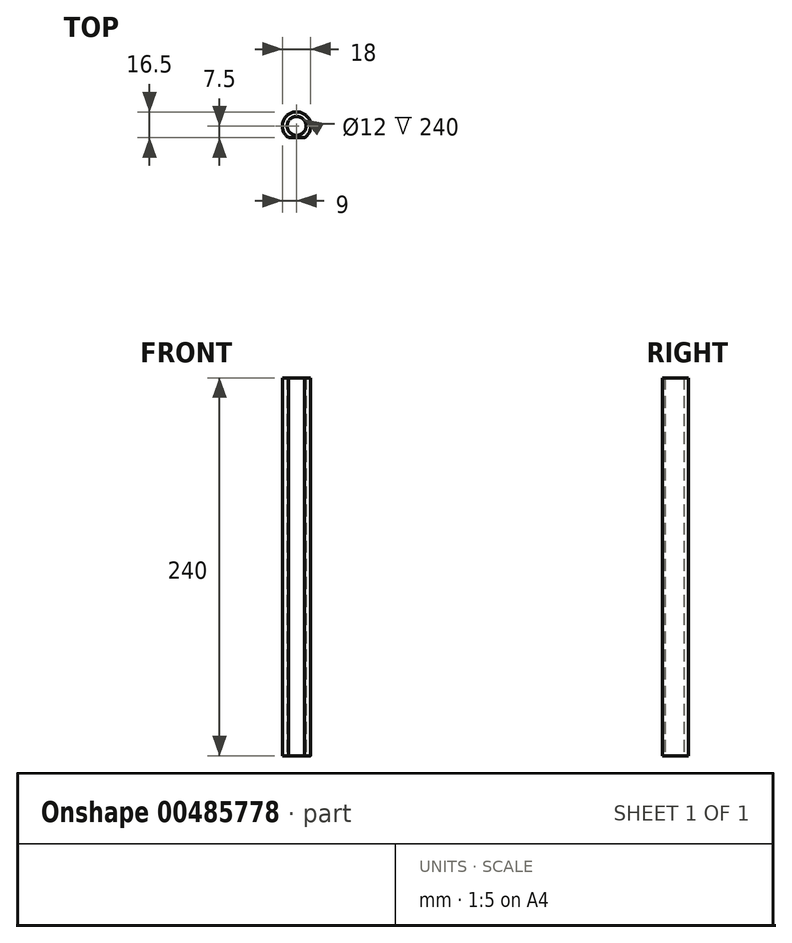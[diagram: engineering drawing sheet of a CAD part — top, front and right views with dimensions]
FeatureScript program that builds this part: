
annotation { "Feature Type Name" : "Feature", "Feature Type Description" : "" }
export const myFeature = defineFeature(function(context is Context, id is Id, definition is map)
    precondition{}
    {
        {
            var Q0;
            Q0=qCreatedBy(makeId("Top.planeOp"),FACE);
            var sketch = newSketch(context, id + "F0", { "sketchPlane" : qUnion([Q0])});
            skCircle(sketch, "E0", {"center": v(0, 0) * mm, "radius": 6 * mm});
            skCircle(sketch, "E1", {"center": v(0, 0) * mm, "radius": 9 * mm});
            skSolve(sketch);
        }
        {
            var Q0;
            Q0 = qSketchRegion(id + "F0", true);
            extrude(context, id + "F1", {"entities" : qUnion([Q0]), "depth" : 240 * mm});
        }
        {
            var Q0;
            Q0=qCreatedBy(makeId("Front.planeOp"),FACE);
            cPlane(context, id + "F2", {"entities" : qUnion([Q0]), "cplaneType" : CPlaneType.OFFSET, "offset" : 9 * mm, "width" : 150 * mm, "height" : 150 * mm});
        }
        {
            var Q0;
            Q0=qCreatedBy(id+"F2.planeOp",FACE);
            var sketch = newSketch(context, id + "F3", { "sketchPlane" : qUnion([Q0])});
            skLineSegment(sketch, "E2.0", {"start": v(-9, 240) * mm, "end": v(9, 240) * mm});
            skLineSegment(sketch, "E3.0", {"start": v(-9, 0) * mm, "end": v(9, 0) * mm});
            skLineSegment(sketch, "E4", {"start": v(9, 0) * mm, "end": v(9, 240) * mm});
            skLineSegment(sketch, "E5", {"start": v(-9, 0) * mm, "end": v(-9, 240) * mm});
            skSolve(sketch);
        }
        {
            var Q0;
            Q0 = qSketchRegion(id + "F3", true);
            extrude(context, id + "F4", {"entities" : qUnion([Q0]), "operationType" : NewBodyOperationType.REMOVE, "oppositeDirection" : true, "depth" : 1.5 * mm});
        }
    });
